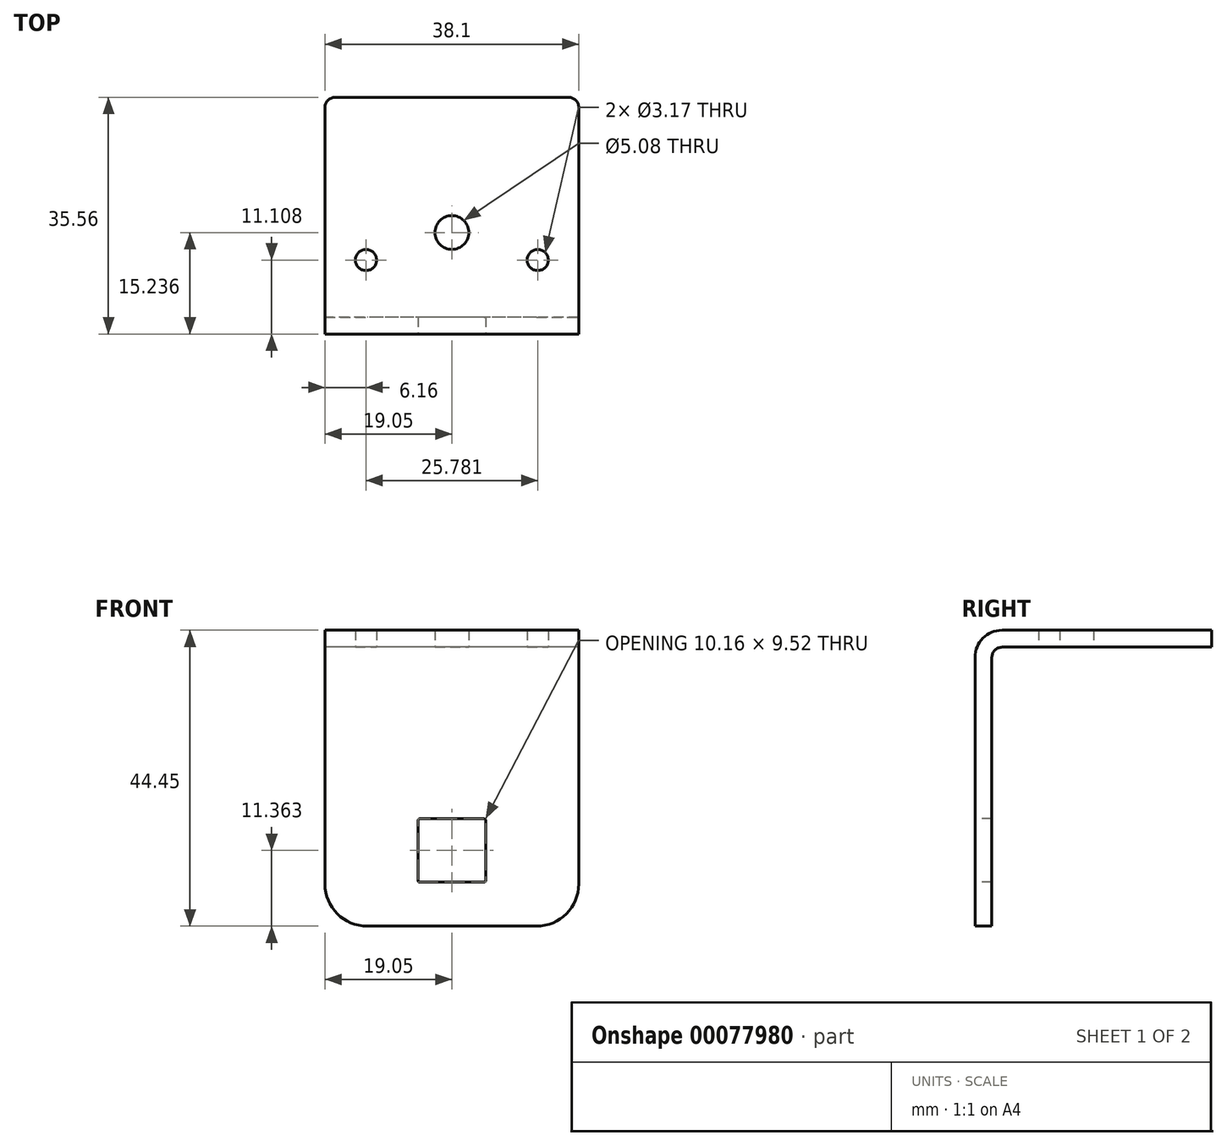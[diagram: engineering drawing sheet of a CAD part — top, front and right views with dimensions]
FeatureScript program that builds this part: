
annotation { "Feature Type Name" : "Feature", "Feature Type Description" : "" }
export const myFeature = defineFeature(function(context is Context, id is Id, definition is map)
    precondition{}
    {
        {
            var Q0;
            Q0=qCreatedBy(makeId("Right.planeOp"),FACE);
            var sketch = newSketch(context, id + "F0", { "sketchPlane" : qUnion([Q0])});
            skLineSegment(sketch, "E0.bottom", {"start": v(-52.32, 1.02) * mm, "end": v(-54.86, 1.02) * mm});
            skLineSegment(sketch, "E0.top", {"start": v(-0.25, 45.47) * mm, "end": v(-50.8, 45.47) * mm});
            skLineSegment(sketch, "E0.left", {"start": v(-0.25, 42.93) * mm, "end": v(-0.25, 45.47) * mm});
            skLineSegment(sketch, "E0.right", {"start": v(-54.86, 1.02) * mm, "end": v(-54.86, 41.4) * mm});
            skLineSegment(sketch, "E1", {"start": v(-52.32, 1.02) * mm, "end": v(-52.32, 41.4) * mm});
            skLineSegment(sketch, "E2", {"start": v(-50.8, 42.93) * mm, "end": v(-0.25, 42.93) * mm});
            skPoint(sketch, "E3.visualSharp", {"position": v(-52.32, 42.93) * mm});
            skArc(sketch, "E3.filletArc", {"start": v(-50.8, 42.93) * mm, "mid": v(-51.88, 42.48) * mm, "end": v(-52.32, 41.4) * mm});
            skPoint(sketch, "E4.visualSharp", {"position": v(-54.86, 45.47) * mm});
            skArc(sketch, "E4.filletArc", {"start": v(-50.8, 45.47) * mm, "mid": v(-53.67, 44.28) * mm, "end": v(-54.86, 41.4) * mm});
            skSolve(sketch);
        }
        {
            var Q0;
            Q0=qSketchRegion(id+"F0",true);
            extrude(context, id + "F1", {"entities" : qUnion([Q0]), "depth" : 38.1 * mm});
        }
        {
            var Q0;
            Q0=makeQuery(id+"F1.opExtrude","CAP_EDGE",EDGE,{"disambiguationData":[OSD([sQuery(id+"F0.wireOp",EDGE,"E0.left")])],"isStart":true});
            var Q1;
            Q1=makeQuery(id+"F1.opExtrude","CAP_EDGE",EDGE,{"disambiguationData":[OSD([sQuery(id+"F0.wireOp",EDGE,"E0.left")])],"isStart":false});
            fillet(context, id + "F2", {"entities" : qUnion([Q0, Q1]), "radius" : 1.52 * mm, "tangentPropagation" : true, "allowEdgeOverflow" : false});
        }
        {
            var Q0;
            Q0=makeQuery(id+"F1.opExtrude","SWEPT_FACE",FACE,{"disambiguationData":[OSD([sQuery(id+"F0.wireOp",EDGE,"E2")])]});
            var sketch = newSketch(context, id + "F3", { "sketchPlane" : qUnion([Q0])});
            skCircle(sketch, "E5", {"center": v(6.16, 43.75) * mm, "radius": 1.59 * mm});
            skCircle(sketch, "E6", {"center": v(19.05, 39.62) * mm, "radius": 2.54 * mm});
            skCircle(sketch, "E7", {"center": v(31.94, 43.75) * mm, "radius": 1.59 * mm});
            skCircle(sketch, "E8", {"center": v(19.05, 7.87) * mm, "radius": 2.54 * mm});
            skLineSegment(sketch, "E9", {"start": v(19.05, 0.25) * mm, "end": v(19.05, 50.8) * mm, "construction": true});
            skLineSegment(sketch, "E10", {"start": v(0, 43.75) * mm, "end": v(38.1, 43.75) * mm, "construction": true});
            skSolve(sketch);
        }
        {
            var Q0;
            Q0=qSketchRegion(id+"F3",true);
            extrude(context, id + "F4", {"entities" : qUnion([Q0]), "operationType" : NewBodyOperationType.REMOVE, "endBound" : BoundingType.UP_TO_NEXT, "oppositeDirection" : true, "depth" : 25.4 * mm});
        }
        {
            var Q0;
            Q0=makeQuery(id+"F1.opExtrude","SWEPT_FACE",FACE,{"disambiguationData":[OSD([sQuery(id+"F0.wireOp",EDGE,"E0.right")])]});
            var sketch = newSketch(context, id + "F5", { "sketchPlane" : qUnion([Q0])});
            skLineSegment(sketch, "E11.bottom", {"start": v(14.22, 7.62) * mm, "end": v(23.88, 7.62) * mm});
            skLineSegment(sketch, "E11.top", {"start": v(14.22, 17.15) * mm, "end": v(23.88, 17.15) * mm});
            skLineSegment(sketch, "E11.left", {"start": v(13.97, 7.87) * mm, "end": v(13.97, 16.9) * mm});
            skLineSegment(sketch, "E11.right", {"start": v(24.13, 7.87) * mm, "end": v(24.13, 16.9) * mm});
            skLineSegment(sketch, "E12", {"start": v(19.05, 1.02) * mm, "end": v(19.05, 7.62) * mm, "construction": true});
            skPoint(sketch, "E13.visualSharp", {"position": v(13.97, 17.15) * mm});
            skArc(sketch, "E13.filletArc", {"start": v(14.22, 17.14) * mm, "mid": v(14.04, 17.07) * mm, "end": v(13.97, 16.9) * mm});
            skPoint(sketch, "E14.visualSharp", {"position": v(24.13, 17.15) * mm});
            skArc(sketch, "E14.filletArc", {"start": v(24.13, 16.9) * mm, "mid": v(24.06, 17.07) * mm, "end": v(23.88, 17.15) * mm});
            skPoint(sketch, "E15.visualSharp", {"position": v(24.13, 7.62) * mm});
            skArc(sketch, "E15.filletArc", {"start": v(23.88, 7.62) * mm, "mid": v(24.06, 7.7) * mm, "end": v(24.13, 7.87) * mm});
            skPoint(sketch, "E16.visualSharp", {"position": v(13.97, 7.62) * mm});
            skArc(sketch, "E16.filletArc", {"start": v(13.97, 7.87) * mm, "mid": v(14.04, 7.7) * mm, "end": v(14.22, 7.62) * mm});
            skSolve(sketch);
        }
        {
            var Q0;
            Q0=qSketchRegion(id+"F5",true);
            extrude(context, id + "F6", {"entities" : qUnion([Q0]), "operationType" : NewBodyOperationType.REMOVE, "endBound" : BoundingType.UP_TO_NEXT, "oppositeDirection" : true, "depth" : 25.4 * mm});
        }
        {
            var Q0;
            Q0=makeQuery(id+"F1.opExtrude","CAP_EDGE",EDGE,{"disambiguationData":[OSD([sQuery(id+"F0.wireOp",EDGE,"E0.bottom")])],"isStart":false});
            var Q1;
            Q1=makeQuery(id+"F1.opExtrude","CAP_EDGE",EDGE,{"disambiguationData":[OSD([sQuery(id+"F0.wireOp",EDGE,"E0.bottom")])],"isStart":true});
            fillet(context, id + "F7", {"entities" : qUnion([Q0, Q1]), "radius" : 6.35 * mm, "tangentPropagation" : true, "allowEdgeOverflow" : false});
        }
        {
            var Q0;
            Q0=makeQuery(id+"F1.opExtrude","SWEPT_FACE",FACE,{"disambiguationData":[OSD([sQuery(id+"F0.wireOp",EDGE,"E0.left")])]});
            var sketch = newSketch(context, id + "F8", { "sketchPlane" : qUnion([Q0])});
            skLineSegment(sketch, "E17.bottom", {"start": v(18.57, 20.53) * mm, "end": v(-138.68, 20.53) * mm});
            skLineSegment(sketch, "E17.top", {"start": v(18.57, 114.65) * mm, "end": v(-138.68, 114.65) * mm});
            skLineSegment(sketch, "E17.left", {"start": v(18.57, 20.53) * mm, "end": v(18.57, 114.65) * mm});
            skLineSegment(sketch, "E17.right", {"start": v(-138.68, 20.53) * mm, "end": v(-138.68, 114.65) * mm});
            skPoint(sketch, "E17.middle", {"position": v(-60.06, 67.59) * mm});
            skSolve(sketch);
        }
        {
            var Q0;
            Q0 = qSketchRegion(id + "F8", true);
            extrude(context, id + "F9", {"entities" : qUnion([Q0]), "operationType" : NewBodyOperationType.REMOVE, "oppositeDirection" : true, "depth" : 19.05 * mm});
        }
        {
            var Q0;
            Q0=makeQuery(id+"F9.boolean.opBoolean","INTERSECT",EDGE,{"derivedFrom":[makeQuery(id+"F1.opExtrude","CAP_FACE",FACE,{"disambiguationData":[OSD([sQuery(id+"F0.wireOp",EDGE,"E0.bottom"),sQuery(id+"F0.wireOp",EDGE,"E0.top"),sQuery(id+"F0.wireOp",EDGE,"E0.left"),sQuery(id+"F0.wireOp",EDGE,"E0.right"),sQuery(id+"F0.wireOp",EDGE,"E1"),sQuery(id+"F0.wireOp",EDGE,"E2"),sQuery(id+"F0.wireOp",EDGE,"E3.filletArc"),sQuery(id+"F0.wireOp",EDGE,"E4.filletArc")])],"isStart":false}),makeQuery(id+"F9.opExtrude","CAP_FACE",FACE,{"disambiguationData":[OSD([sQuery(id+"F8.wireOp",EDGE,"E17.bottom"),sQuery(id+"F8.wireOp",EDGE,"E17.top"),sQuery(id+"F8.wireOp",EDGE,"E17.left"),sQuery(id+"F8.wireOp",EDGE,"E17.right")])],"isStart":false})]});
            var Q1;
            Q1=makeQuery(id+"F9.boolean.opBoolean","INTERSECT",EDGE,{"derivedFrom":[makeQuery(id+"F1.opExtrude","CAP_FACE",FACE,{"disambiguationData":[OSD([sQuery(id+"F0.wireOp",EDGE,"E0.bottom"),sQuery(id+"F0.wireOp",EDGE,"E0.top"),sQuery(id+"F0.wireOp",EDGE,"E0.left"),sQuery(id+"F0.wireOp",EDGE,"E0.right"),sQuery(id+"F0.wireOp",EDGE,"E1"),sQuery(id+"F0.wireOp",EDGE,"E2"),sQuery(id+"F0.wireOp",EDGE,"E3.filletArc"),sQuery(id+"F0.wireOp",EDGE,"E4.filletArc")])],"isStart":true}),makeQuery(id+"F9.opExtrude","CAP_FACE",FACE,{"disambiguationData":[OSD([sQuery(id+"F8.wireOp",EDGE,"E17.bottom"),sQuery(id+"F8.wireOp",EDGE,"E17.top"),sQuery(id+"F8.wireOp",EDGE,"E17.left"),sQuery(id+"F8.wireOp",EDGE,"E17.right")])],"isStart":false})]});
            fillet(context, id + "F10", {"entities" : qUnion([Q0, Q1]), "radius" : 1.52 * mm, "tangentPropagation" : true, "allowEdgeOverflow" : false});
        }
    });
